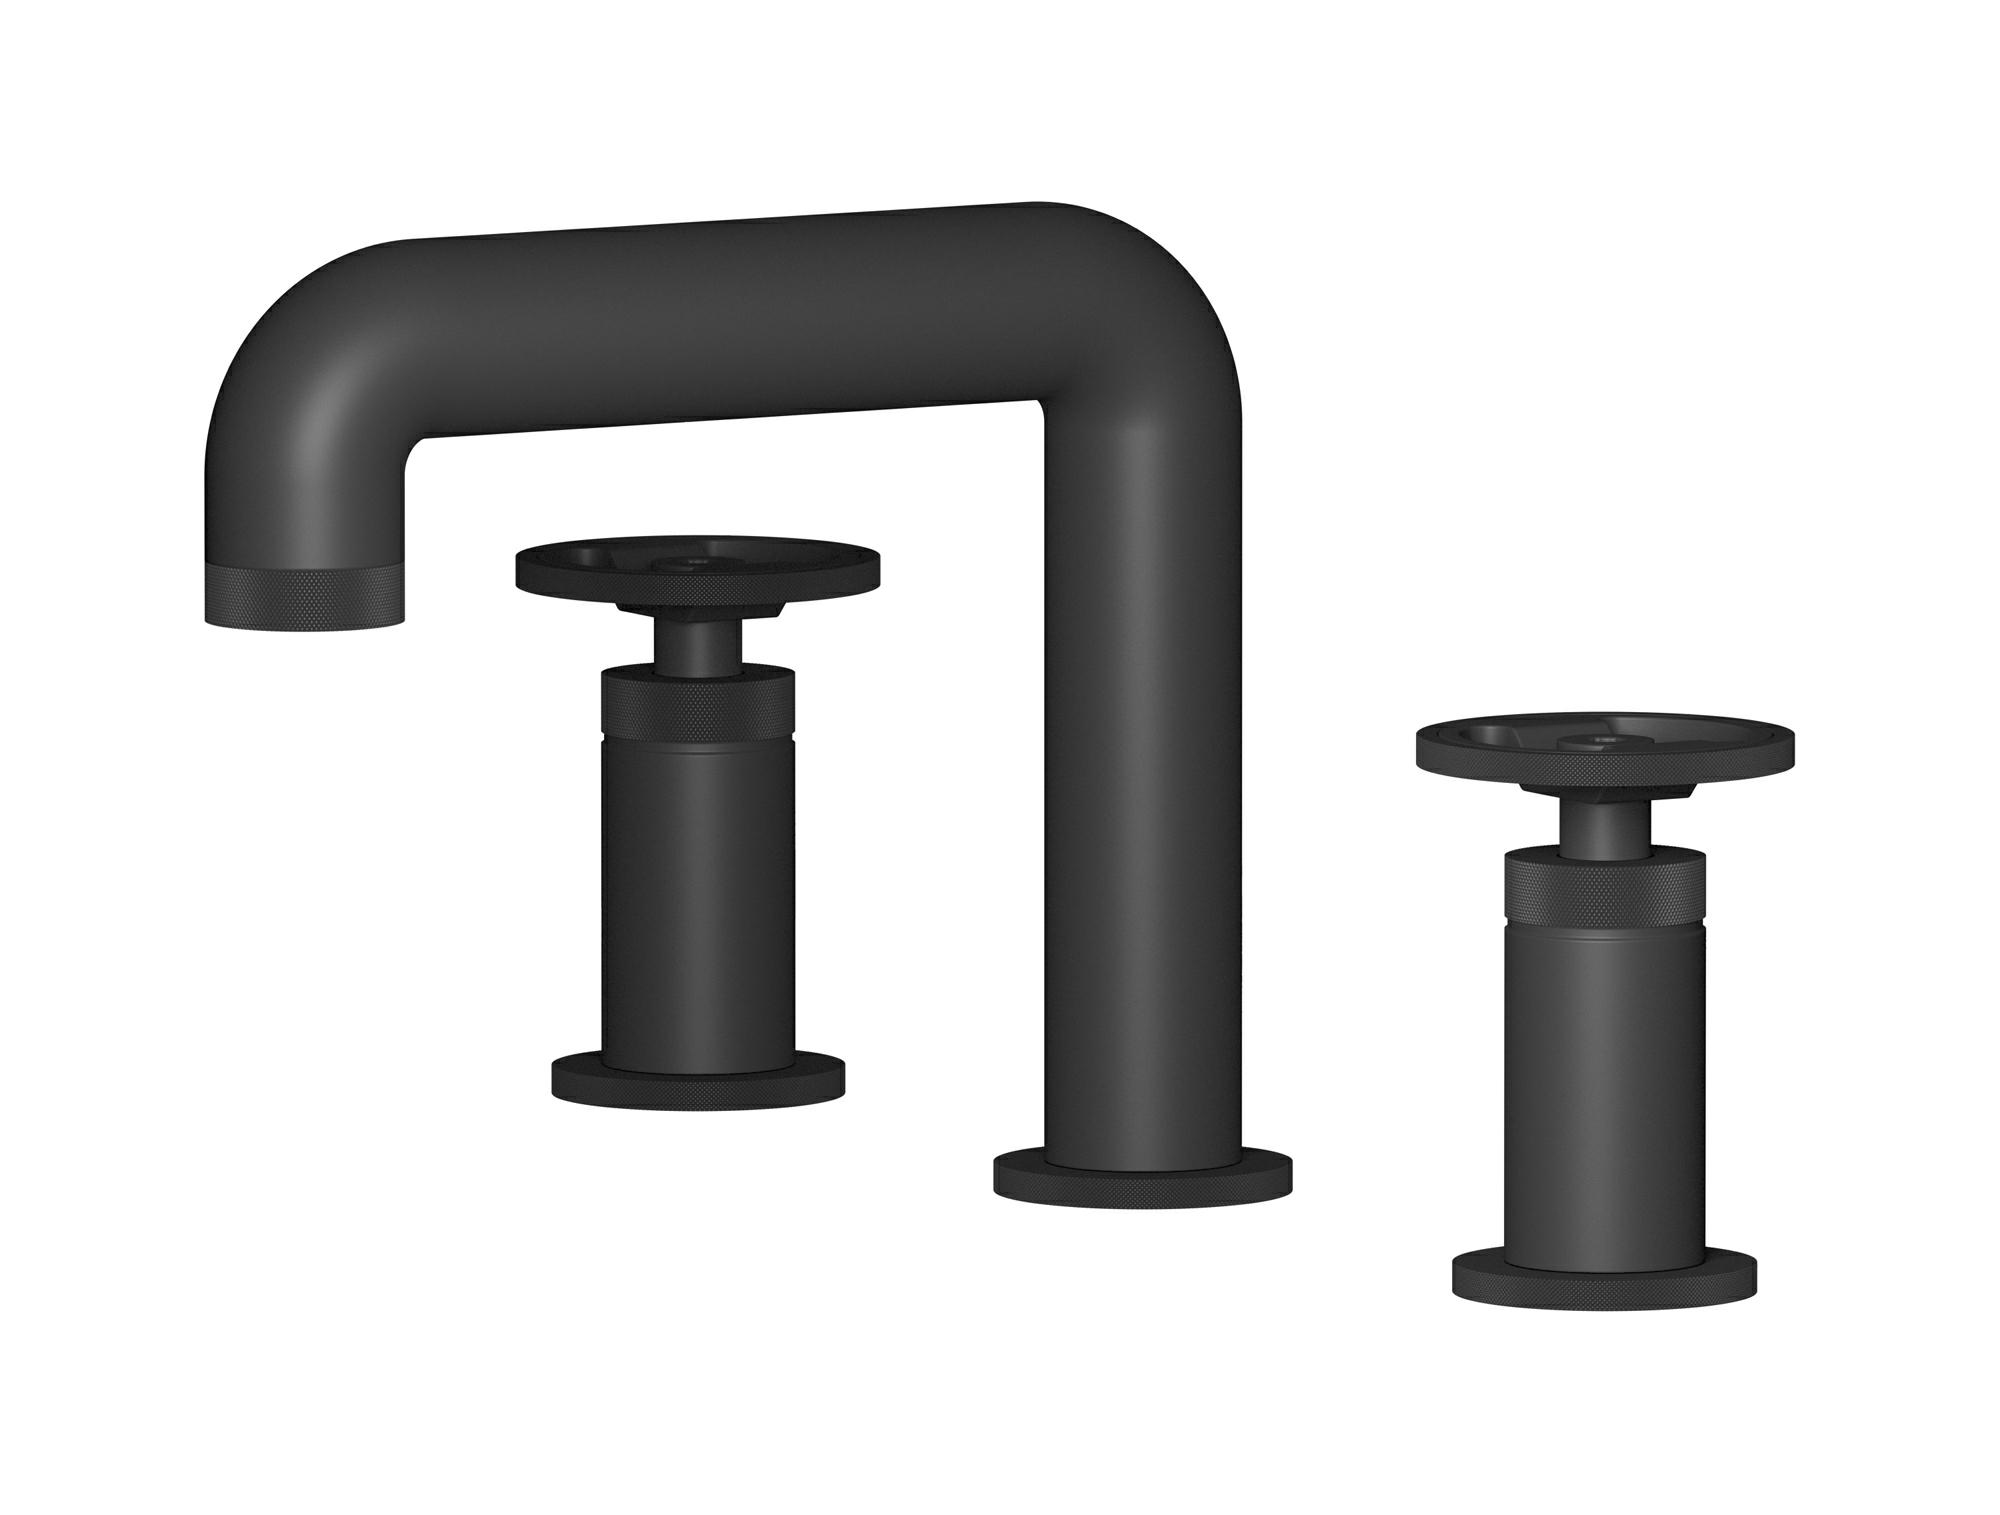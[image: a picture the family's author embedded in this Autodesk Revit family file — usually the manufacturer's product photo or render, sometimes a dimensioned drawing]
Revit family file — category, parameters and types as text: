
# Revit family: B1392
name_source: partatom
category: Apparecchi idraulici
units: mm (PartAtom-declared; Revit-internal decimal feet)

## family parameters
Basato su piano di lavoro = No
Condiviso = No
Mantieni orientamento annotazione = No
Numero OmniClass = 23.45.55.17
Punto di calcolo locali = No
Quota connettore circolare = Usa diametro
Sempre verticale = Sì
Taglio con vuoti quando caricato = No
Tipo di parte = Normale
Titolo OmniClass = Mixing Faucets

## types (13) — shared parameters
Cold water inlet = 10 mm  [stored 0.0328084 ft]
Commenti sul tipo = Three holes washbasin set with low spout
Connessione CW = No
Connessione HW = No
Connessione di scarico = No
Connessione di ventilazione = No
Descrizione = Three holes washbasin set with low spout
Hot water inlet = 10 mm  [stored 0.0328084 ft]
Produttore = IB Rubinetterie S.p.A.
URL = https://www.weareib.it
zero-valued in all types: Prospetto di default

## per-type parameters (varying)
| type | Finishes surface | Immagine tipo | Modello |
| Chrome | IB_Chrome | B1392CC.jpg | B1392CC |
| Black Chrome | IB_Black chrome | B1392CF.jpg | B1392CF |
| Brushed Black Chrome | IB_Brushed black chrome | B1392CS.jpg | B1392CS |
| Pale Gold | IB_Pale gold | B1392II.jpg | B1392II |
| Brushed Pale Gold | IB_brushed pale gold | B1392IS.jpg | B1392IS |
| Matt Black | IB_matt black | B1392NP.jpg | B1392NP |
| Natural Brass | IB_Brass | B1392ON.jpg | B1392ON |
| Gold | IB_gold | B1392OO.jpg | B1392OO |
| Brushed Gold | IB_brushed gold | B1392OS.jpg | B1392OS |
| Rose Gold | IB_Rose gold | B1392RS.jpg | B1392RS |
| Brushed Rose Gold | IB_Brushed rose gold | B1392SR.jpg | B1392SR |
| Brushed Nickel | IB_Brushed nickel | B1392SS.jpg | B1392SS |
| Modern Bronze | IB_Modern bronze | B1392MB.jpg | B1392MB |

note: [stored X ft] marks values corroborated as IEEE doubles in the binary element streams (Revit-internal decimal feet)
